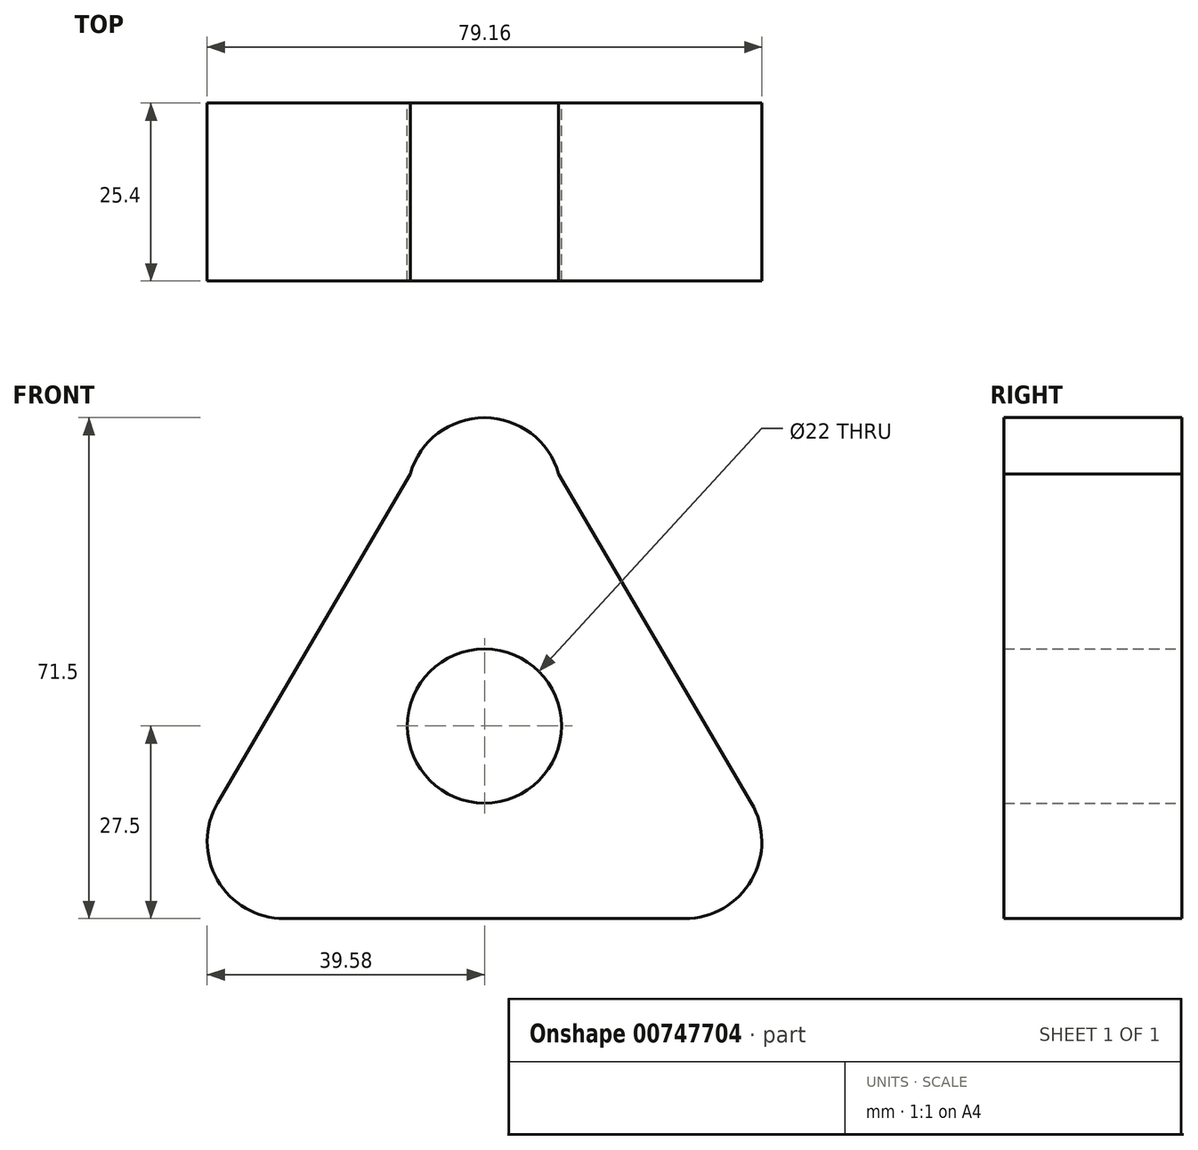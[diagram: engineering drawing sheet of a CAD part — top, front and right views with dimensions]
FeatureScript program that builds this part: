
annotation { "Feature Type Name" : "Feature", "Feature Type Description" : "" }
export const myFeature = defineFeature(function(context is Context, id is Id, definition is map)
    precondition{}
    {
        {
            var Q0;
            Q0=qCreatedBy(makeId("Front.planeOp"),FACE);
            var sketch = newSketch(context, id + "F0", { "sketchPlane" : qUnion([Q0])});
            skCircle(sketch, "E0", {"center": v(0, 0) * mm, "radius": 11 * mm});
            skLineSegment(sketch, "E1", {"start": v(0, 0) * mm, "end": v(0, 33) * mm});
            skLineSegment(sketch, "E2.1.0", {"start": v(0, 0) * mm, "end": v(-28.58, -16.5) * mm});
            skLineSegment(sketch, "E2.2.0", {"start": v(0, 0) * mm, "end": v(28.58, -16.5) * mm});
            skCircle(sketch, "E3", {"center": v(-28.58, -16.5) * mm, "radius": 11 * mm});
            skCircle(sketch, "E4", {"center": v(28.58, -16.5) * mm, "radius": 11 * mm});
            skCircle(sketch, "E5", {"center": v(0, 33) * mm, "radius": 11 * mm});
            skLineSegment(sketch, "E6", {"start": v(-10.58, 35.99) * mm, "end": v(-38.07, -10.94) * mm});
            skLineSegment(sketch, "E7", {"start": v(10.58, 35.99) * mm, "end": v(38.07, -10.94) * mm});
            skLineSegment(sketch, "E8", {"start": v(-28.58, -27.5) * mm, "end": v(28.58, -27.5) * mm});
            skSolve(sketch);
        }
        {
            var Q0;
            Q0 = qSketchRegion(id + "F0", true);
            extrude(context, id + "F1", {"entities" : qUnion([Q0]), "depth" : 25.4 * mm, "offsetDistance" : 25.4 * mm});
        }
    });
